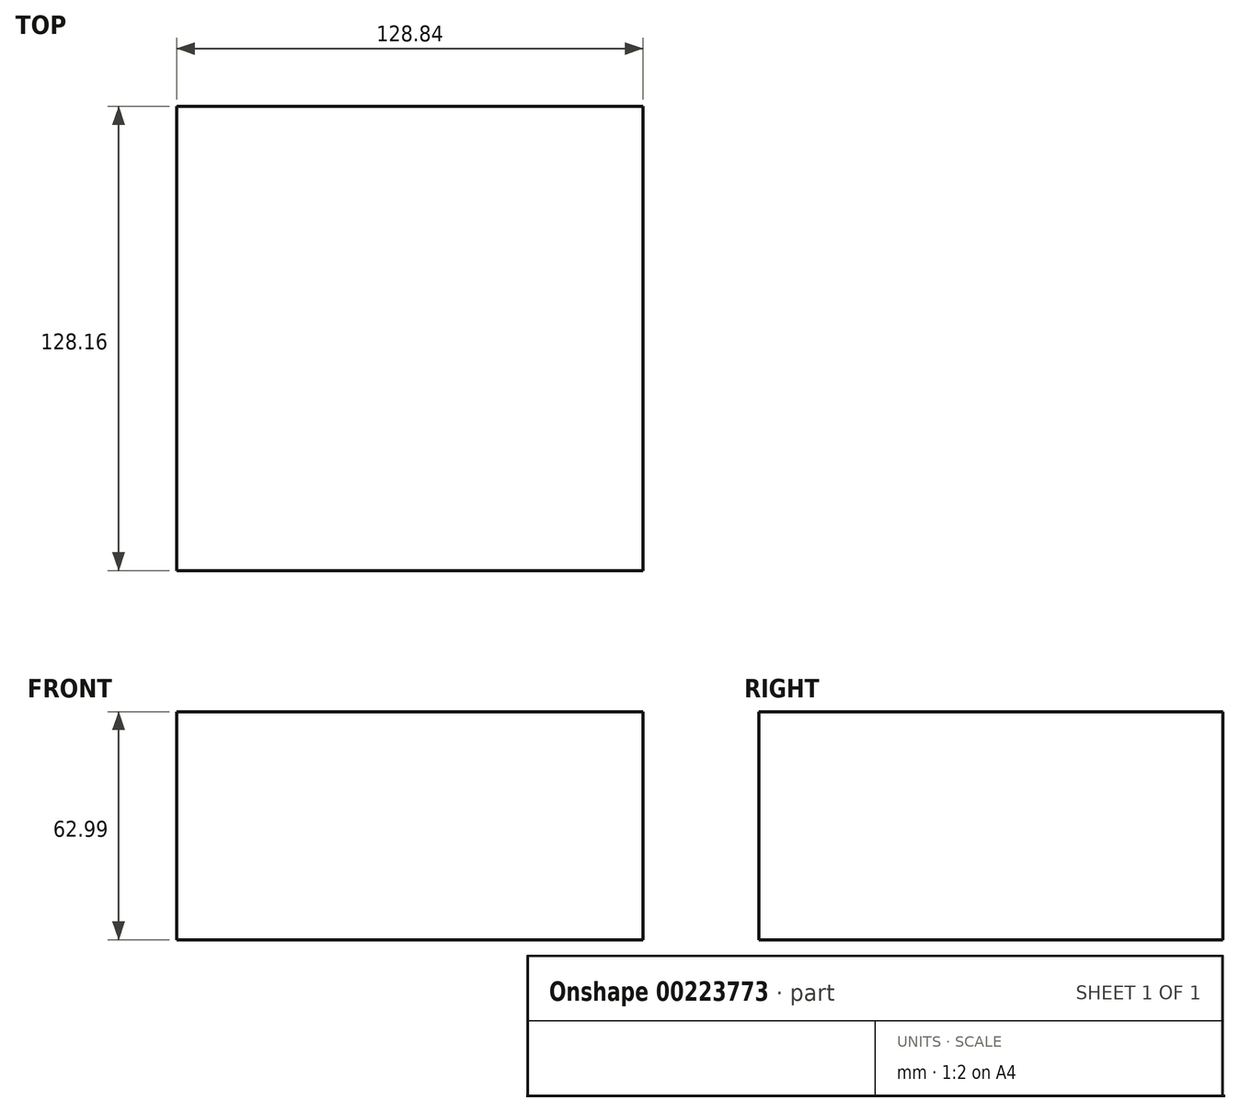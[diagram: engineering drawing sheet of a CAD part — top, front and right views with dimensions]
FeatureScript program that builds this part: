
annotation { "Feature Type Name" : "Feature", "Feature Type Description" : "" }
export const myFeature = defineFeature(function(context is Context, id is Id, definition is map)
    precondition{}
    {
        {
            var Q0;
            Q0=qCreatedBy(makeId("Top.planeOp"),FACE);
            var sketch = newSketch(context, id + "F0", { "sketchPlane" : qUnion([Q0])});
            skLineSegment(sketch, "E0.bottom", {"start": v(-64.42, 64.08) * mm, "end": v(64.42, 64.08) * mm});
            skLineSegment(sketch, "E0.top", {"start": v(-64.42, -64.08) * mm, "end": v(64.42, -64.08) * mm});
            skLineSegment(sketch, "E0.left", {"start": v(-64.42, 64.08) * mm, "end": v(-64.42, -64.08) * mm});
            skLineSegment(sketch, "E0.right", {"start": v(64.42, 64.08) * mm, "end": v(64.42, -64.08) * mm});
            skPoint(sketch, "E0.middle", {"position": v(0, 0) * mm});
            skSolve(sketch);
        }
        {
            var Q0;
            Q0=makeQuery(id+"F0.imprint","IMPRINT",FACE,{"disambiguationData":[TD([[makeQuery(id+"F0.imprint","IMPRINT",EDGE,{"derivedFrom":sQuery(id+"F0.wireOp",EDGE,"E0.bottom")}),-1.0]])]});
            var sketch = newSketch(context, id + "F1", { "sketchPlane" : qUnion([Q0])});
            skCircle(sketch, "E1", {"center": v(-50.57, 0) * mm, "radius": 10.3 * mm});
            skSolve(sketch);
        }
        {
            var Q0;
            Q0=makeQuery(id+"F0.imprint","IMPRINT",FACE,{"disambiguationData":[TD([[makeQuery(id+"F0.imprint","IMPRINT",EDGE,{"derivedFrom":sQuery(id+"F0.wireOp",EDGE,"E0.bottom")}),-1.0]])]});
            var sketch = newSketch(context, id + "F2", { "sketchPlane" : qUnion([Q0])});
            skLineSegment(sketch, "E2", {"start": v(0, 64.3) * mm, "end": v(0, -64.08) * mm});
            skSolve(sketch);
        }
        {
            var Q0;
            Q0=sQuery(id+"F1.wireOp",EDGE,"E1");
            var Q1;
            Q1=sQuery(id+"F2.wireOp",EDGE,"E2");
            revolve(context, id + "F3", {"bodyType" : ToolBodyType.SURFACE, "surfaceEntities" : qUnion([Q0]), "axis" : qUnion([Q1]), "revolveType" : RevolveType.FULL});
        }
        {
            var Q0;
            Q0 = qSketchRegion(id + "F0", true);
            extrude(context, id + "F4", {"entities" : qUnion([Q0]), "oppositeDirection" : true, "depth" : 63 * mm});
        }
    });
